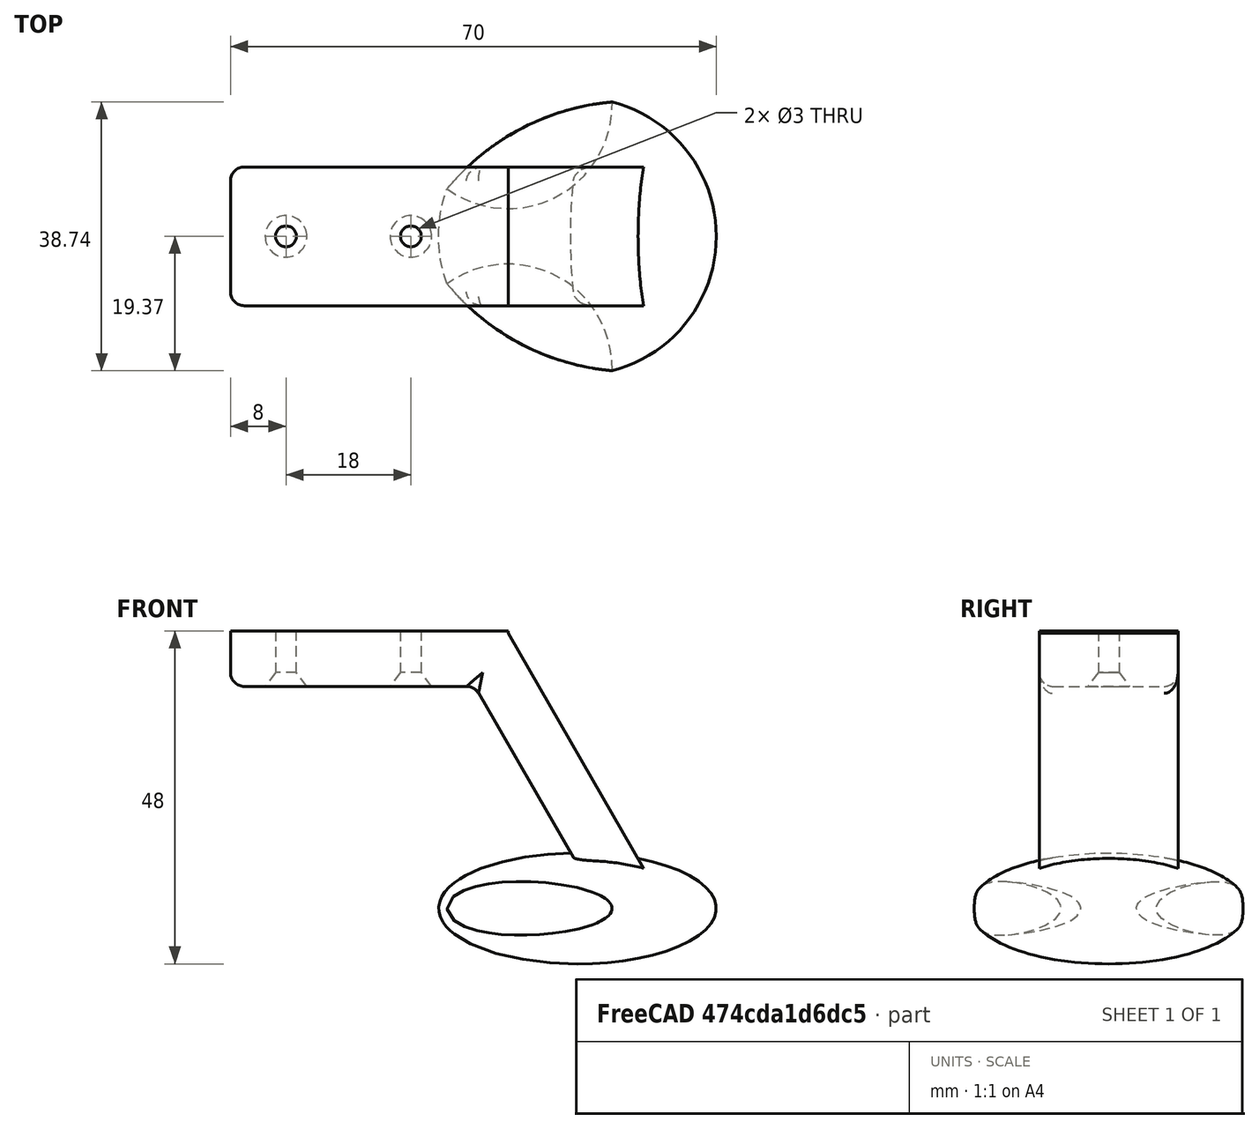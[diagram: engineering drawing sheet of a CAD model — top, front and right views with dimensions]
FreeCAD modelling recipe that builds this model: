
FCSTD DOCUMENT  (FreeCAD 0.20R28811 (Git))
Label: Mickey_SAM
License: All rights reserved
LicenseURL: http://en.wikipedia.org/wiki/All_rights_reserved
objects: Part::Cut×4, Part::Ellipsoid×3, Part::MultiFuse×3, Part::Box×2, Part::Fillet×2, Part::Cylinder×2, Part::Cone×2, App::LinkGroup×1
note: 18 computed .brp shape members not serialized (recipe doc carries the construction recipe); baked Part::Feature solids carry a one-line shape summary decoded from their .brp

FEATURE [Part::Ellipsoid] Ellipsoid
  Angle1 = -90
  Angle2 = 90
  Angle3 = 360
  AttacherType = Attacher::AttachEngine3D
  Radius1 = 8
  Radius2 = 20
  Radius3 = 20
FEATURE [Part::Ellipsoid] Ellipsoid001
  Angle1 = -90
  Angle2 = 90
  Angle3 = 360
  AttacherType = Attacher::AttachEngine3D
  Placement = pos=(-10,-19,0) rot=(0,0,1;0rad)
  Radius1 = 4
  Radius2 = 15
  Radius3 = 15
FEATURE [Part::Ellipsoid] Ellipsoid002
  Angle1 = -90
  Angle2 = 90
  Angle3 = 360
  AttacherType = Attacher::AttachEngine3D
  Placement = pos=(-10,19,0) rot=(0,0,1;0rad)
  Radius1 = 4
  Radius2 = 15
  Radius3 = 15
FEATURE [App::LinkGroup] LinkGroup
  ElementList = -> [Ellipsoid002,Ellipsoid001,Ellipsoid]
  LinkMode = 0
FEATURE [Part::Box] Box  label="Cube"
  AttacherType = Attacher::AttachEngine3D
  Height = 8
  Length = 40
  Placement = pos=(-50,-10,32) rot=(0,0,1;0rad)
  Width = 20
FEATURE [Part::Box] Box001  label="Cube001"
  AttacherType = Attacher::AttachEngine3D
  Height = 8
  Length = 40
  Placement = pos=(10,-10,5) rot=(0,1,0;4.18879rad)
  Width = 20
FEATURE [Part::MultiFuse] Fusion
  Refine = true
  Shapes = -> [Box001,Box]
FEATURE [Part::Fillet] Fillet
  Base = -> Fusion
  Edges = 7 edges r=2: [Edge5,Edge7,Edge11,Edge12,Edge13,Edge17,Edge19]
FEATURE [Part::Fillet] Fillet001
  Base = -> Fillet
  Edges = 1 edges r=2: [Edge17]
FEATURE [Part::Cylinder] Cylinder
  Angle = 360
  AttacherType = Attacher::AttachEngine3D
  FirstAngle = 0
  Height = 10
  Placement = pos=(-42,0,31) rot=(0,0,1;0rad)
  Radius = 1.5
  SecondAngle = 0
FEATURE [Part::Cylinder] Cylinder001
  Angle = 360
  AttacherType = Attacher::AttachEngine3D
  FirstAngle = 0
  Height = 10
  Placement = pos=(-24,0,31) rot=(0,0,1;0rad)
  Radius = 1.5
  SecondAngle = 0
FEATURE [Part::Cone] Cone
  Angle = 360
  AttacherType = Attacher::AttachEngine3D
  Height = 2
  Placement = pos=(-24,0,32) rot=(0,0,1;0rad)
  Radius1 = 3
  Radius2 = 1.5
FEATURE [Part::Cone] Cone001
  Angle = 360
  AttacherType = Attacher::AttachEngine3D
  Height = 2
  Placement = pos=(-42,0,32) rot=(0,0,1;0rad)
  Radius1 = 3
  Radius2 = 1.5
FEATURE [Part::Cut] Cut
  Base = -> Fillet001
  Refine = true
  Tool = -> Cylinder
FEATURE [Part::Cut] Cut001
  Base = -> Cut
  Refine = true
  Tool = -> Cylinder001
FEATURE [Part::Cut] Cut002
  Base = -> Cut001
  Refine = true
  Tool = -> Cone
FEATURE [Part::Cut] Cut003
  Base = -> Cut002
  Refine = true
  Tool = -> Cone001
FEATURE [Part::MultiFuse] Fusion001
  Refine = true
  Shapes = -> [Ellipsoid002,Ellipsoid,Ellipsoid001]
FEATURE [Part::MultiFuse] Fusion002
  Refine = true
  Shapes = -> [Cut003,Fusion001]
